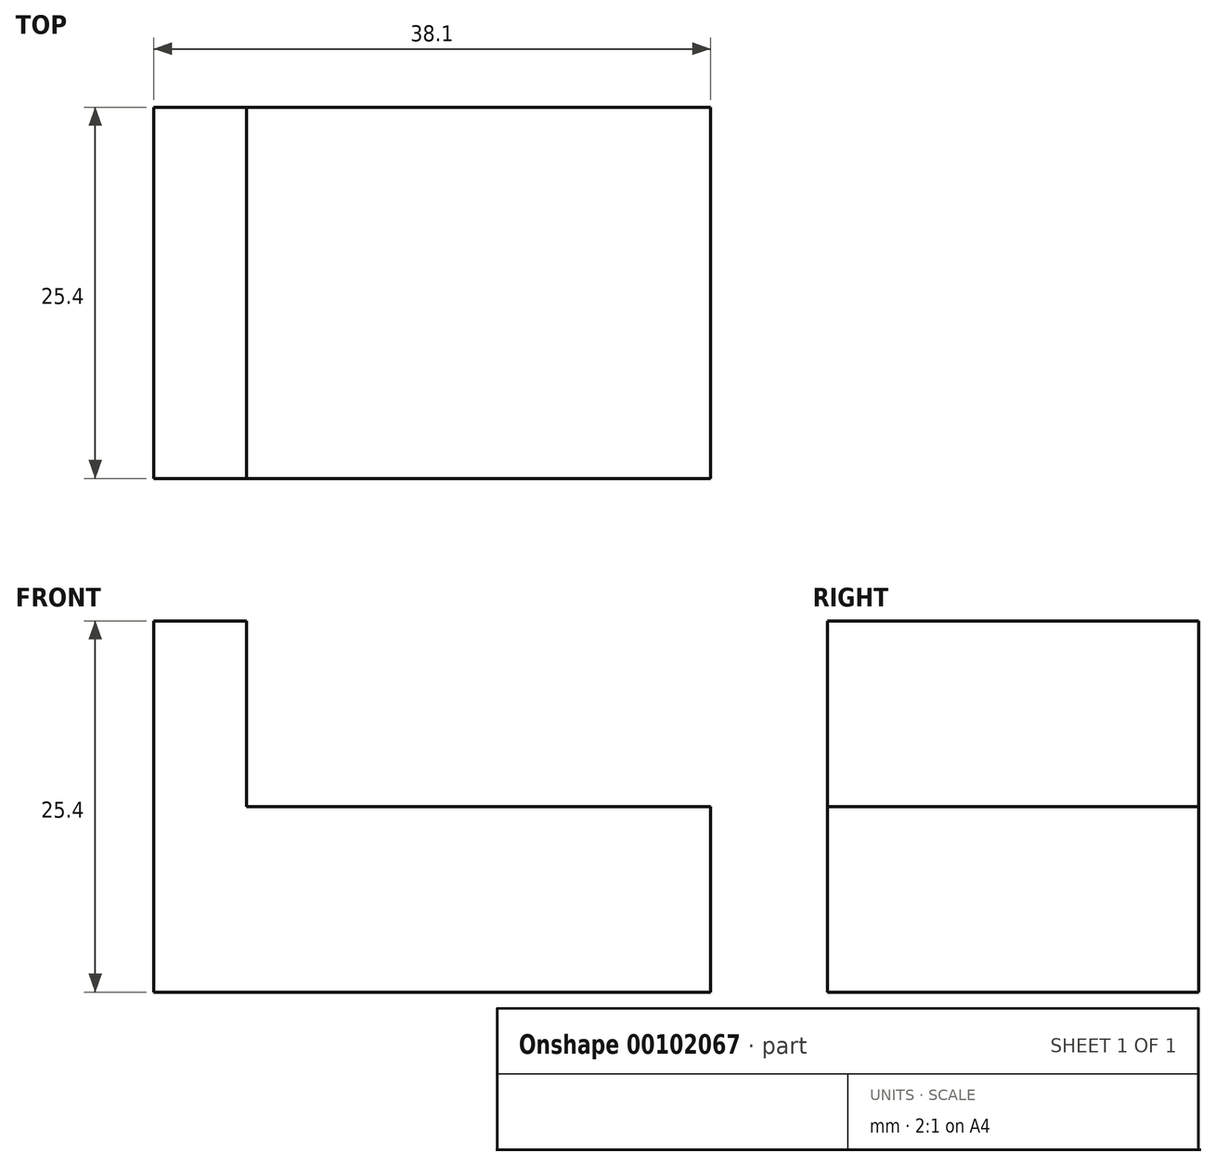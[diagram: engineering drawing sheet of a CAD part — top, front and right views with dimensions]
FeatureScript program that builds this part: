
annotation { "Feature Type Name" : "Feature", "Feature Type Description" : "" }
export const myFeature = defineFeature(function(context is Context, id is Id, definition is map)
    precondition{}
    {
        {
            var Q0;
            Q0=qCreatedBy(makeId("Front.planeOp"),FACE);
            var sketch = newSketch(context, id + "F0", { "sketchPlane" : qUnion([Q0])});
            skLineSegment(sketch, "E0", {"start": v(0, 0) * mm, "end": v(0, 25.4) * mm});
            skLineSegment(sketch, "E1", {"start": v(0, 25.4) * mm, "end": v(6.35, 25.4) * mm});
            skLineSegment(sketch, "E2", {"start": v(6.35, 25.4) * mm, "end": v(6.35, 12.7) * mm});
            skLineSegment(sketch, "E3", {"start": v(6.35, 12.7) * mm, "end": v(38.1, 12.7) * mm});
            skLineSegment(sketch, "E4", {"start": v(38.1, 12.7) * mm, "end": v(38.1, 0) * mm});
            skLineSegment(sketch, "E5", {"start": v(38.1, 0) * mm, "end": v(0, 0) * mm});
            skSolve(sketch);
        }
        {
            var Q0;
            Q0 = qSketchRegion(id + "F0", true);
            extrude(context, id + "F1", {"entities" : qUnion([Q0]), "endBound" : BoundingType.SYMMETRIC, "depth" : 25.4 * mm});
        }
    });
